# Revit family: 1456xxx - Taiko 400
name_source: partatom
category: Lighting Fixtures
units: mm (PartAtom-declared; Revit-internal decimal feet)

## family parameters
Always vertical = Yes
Cut with Voids When Loaded = No
Host = Ceiling
Light Source = No
Maintain Annotation Orientation = No
OmniClass Number = 23.80.70.11
OmniClass Title = Luminaries for Internal Lighting
Part Type = Normal
Room Calculation Point = No
Round Connector Dimension = Use Diameter
Shared = No

## types (2) — shared parameters
Apparent Load = 0 VA
Dimmable = Yes
Dimming Method = Lamp Dependent
Driver Required = No
Efficacy (lm/w) = Lamp Dependent
Lamp = LED
Main Finish = Various
Main Material = Metal - Mild Steel
Manufacturer URL - Europe and Rest of World = www.astrolighting.com
Manufacturer URL - North America = us.astrolighting.com
Power (Watts) = Lamp Dependent
Product Dimensions (MM) = 150 x 400
Product Location = Indoor
Product Name = Taiko 400
Product SKU = 1456xxx
Product Weight (KG) = 3 mm  [stored 0.00984252 ft]
zero-valued in all types: Default Elevation

## per-type parameters (varying)
| type | ADA compliant | Electrical Class | Location / IP Rating |
| CE |  | CE (Class 1) | IP20 |
| ETL | Yes - if installed in compliance with ADA §307.4 |  |  |

note: [stored X ft] marks values corroborated as IEEE doubles in the binary element streams (Revit-internal decimal feet)

## geometry (parser evidence)
native form markers: Sweep x3
no freeform markers — native parametric forms only
